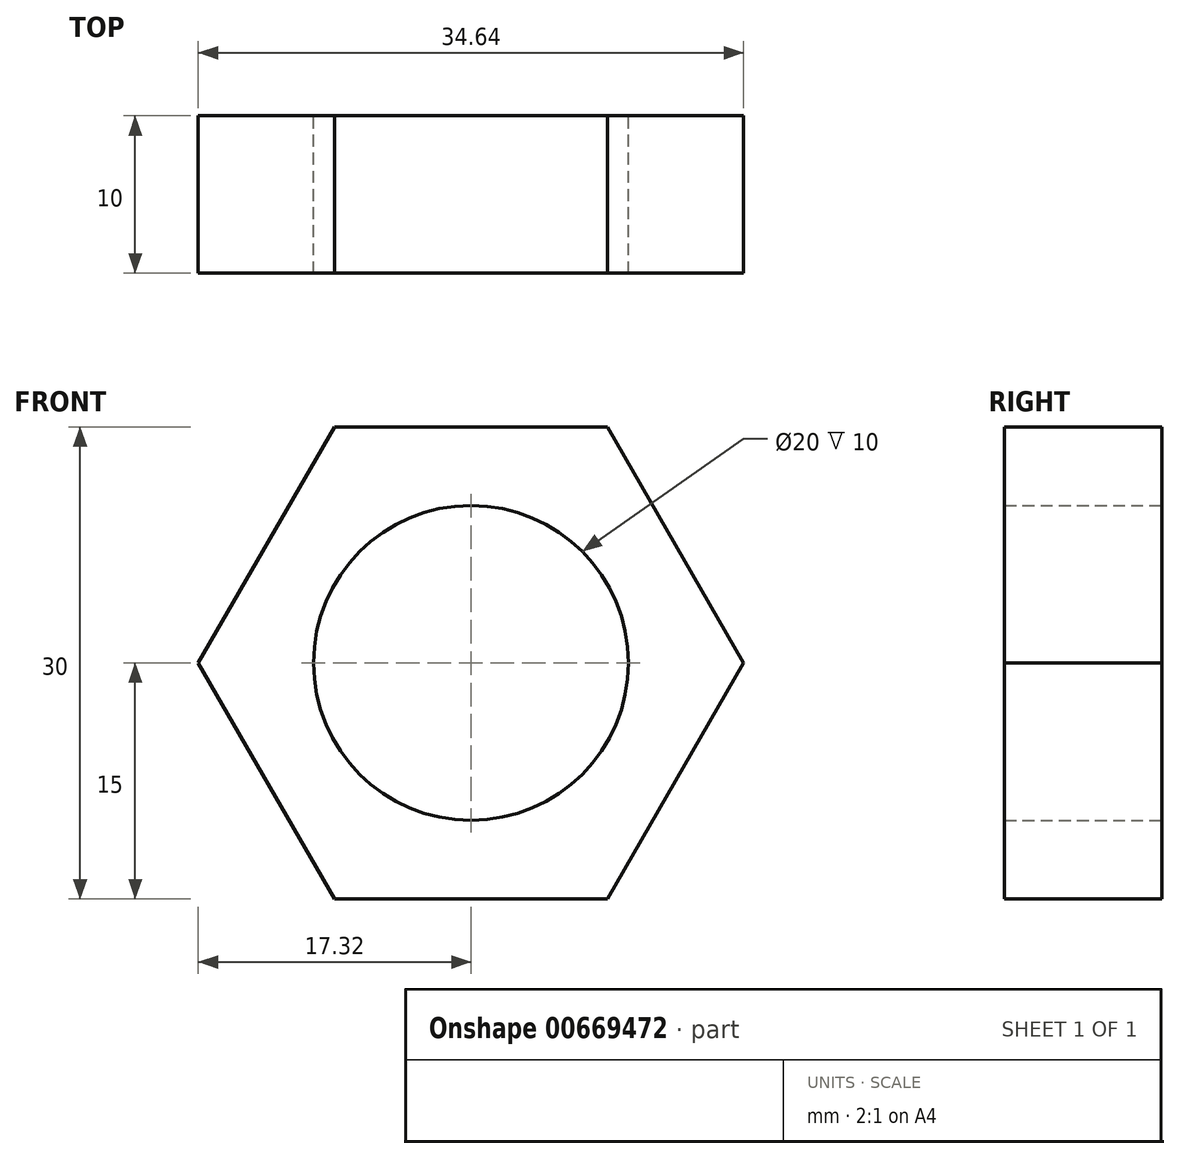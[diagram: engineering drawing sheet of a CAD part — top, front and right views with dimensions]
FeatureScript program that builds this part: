
annotation { "Feature Type Name" : "Feature", "Feature Type Description" : "" }
export const myFeature = defineFeature(function(context is Context, id is Id, definition is map)
    precondition{}
    {
        {
            var Q0;
            Q0=qCreatedBy(makeId("Front.planeOp"),FACE);
            var sketch = newSketch(context, id + "F0", { "sketchPlane" : qUnion([Q0])});
            skCircle(sketch, "E0.cCircle", {"center": v(0, 0) * mm, "radius": 15 * mm, "construction": true});
            skLineSegment(sketch, "E0.0", {"start": v(8.66, -15) * mm, "end": v(-8.66, -15) * mm});
            skLineSegment(sketch, "E0.1", {"start": v(-8.66, -15) * mm, "end": v(-17.32, 0) * mm});
            skLineSegment(sketch, "E0.2", {"start": v(-17.32, 0) * mm, "end": v(-8.66, 15) * mm});
            skLineSegment(sketch, "E0.3", {"start": v(-8.66, 15) * mm, "end": v(8.66, 15) * mm});
            skLineSegment(sketch, "E0.4", {"start": v(8.66, 15) * mm, "end": v(17.32, 0) * mm});
            skLineSegment(sketch, "E0.5", {"start": v(17.32, 0) * mm, "end": v(8.66, -15) * mm});
            skPoint(sketch, "E0.0.midPoint", {"position": v(0, -15) * mm});
            skCircle(sketch, "E1", {"center": v(0, 0) * mm, "radius": 10 * mm});
            skSolve(sketch);
        }
        {
            var Q0;
            Q0=makeQuery(id+"F0.imprint","IMPRINT",FACE,{"disambiguationData":[TD([[makeQuery(id+"F0.imprint","IMPRINT",EDGE,{"derivedFrom":sQuery(id+"F0.wireOp",EDGE,"E0.0")}),-1.0]])]});
            extrude(context, id + "F1", {"entities" : qUnion([Q0]), "depth" : 10 * mm, "offsetDistance" : 25 * mm});
        }
    });
